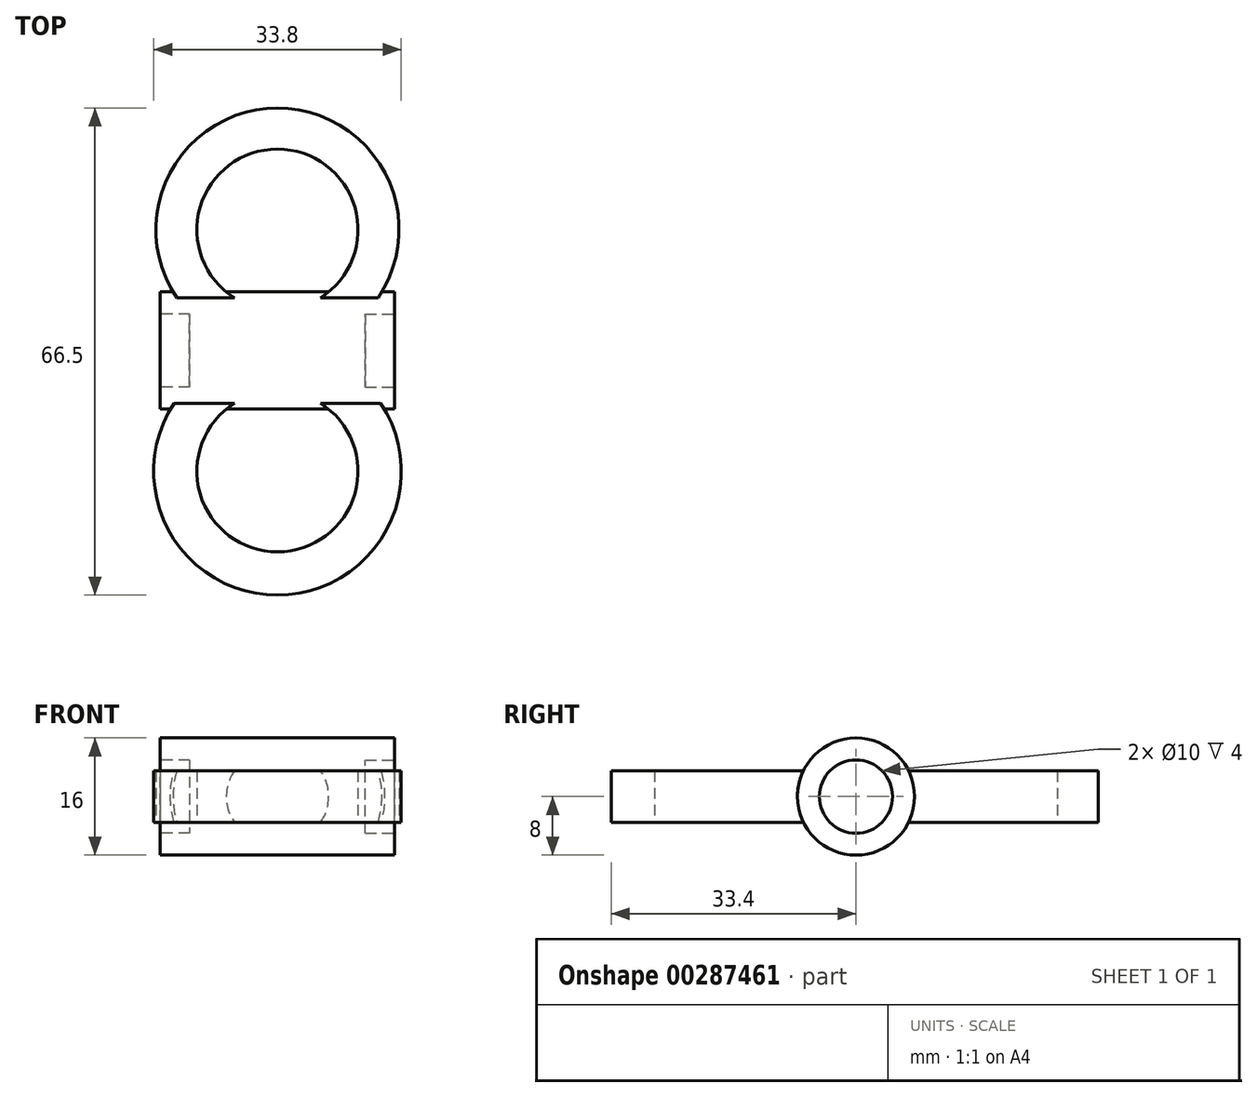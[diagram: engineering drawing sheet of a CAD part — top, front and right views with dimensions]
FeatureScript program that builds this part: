
annotation { "Feature Type Name" : "Feature", "Feature Type Description" : "" }
export const myFeature = defineFeature(function(context is Context, id is Id, definition is map)
    precondition{}
    {
        {
            var Q0;
            Q0=qCreatedBy(makeId("Top.planeOp"),FACE);
            var sketch = newSketch(context, id + "F0", { "sketchPlane" : qUnion([Q0])});
            skCircle(sketch, "E0", {"center": v(0, 0) * mm, "radius": 11 * mm});
            skCircle(sketch, "E1", {"center": v(0, 33) * mm, "radius": 11 * mm});
            skArc(sketch, "E2", {"start": v(13.15, 22.88) * mm, "mid": v(0, 49.6) * mm, "end": v(-13.15, 22.88) * mm});
            skLineSegment(sketch, "E3", {"start": v(0, 16.9) * mm, "end": v(0, 16.65) * mm});
            skArc(sketch, "E4", {"start": v(-13.15, 22.88) * mm, "mid": v(-14.55, 16.72) * mm, "end": v(-13.2, 10.55) * mm});
            skArc(sketch, "E5.trimOffspring", {"start": v(13.2, 10.55) * mm, "mid": v(14.55, 16.72) * mm, "end": v(13.15, 22.88) * mm});
            skArc(sketch, "E6.trimOffspring", {"start": v(-13.2, 10.55) * mm, "mid": v(0, -16.9) * mm, "end": v(13.2, 10.55) * mm});
            skPoint(sketch, "E7.orphan", {"position": v(0, 16.4) * mm});
            skSolve(sketch);
        }
        {
            var Q0;
            Q0=qSketchRegion(id+"F0",true);
            extrude(context, id + "F1", {"entities" : qUnion([Q0]), "depth" : 7 * mm});
        }
        {
            var Q0;
            Q0=qCreatedBy(makeId("Right.planeOp"),FACE);
            var sketch = newSketch(context, id + "F2", { "sketchPlane" : qUnion([Q0])});
            skLineSegment(sketch, "E8", {"start": v(0, 0) * mm, "end": v(0, 7) * mm});
            skLineSegment(sketch, "E9", {"start": v(0, 7) * mm, "end": v(16.5, 7) * mm});
            skLineSegment(sketch, "E10", {"start": v(16.5, 7) * mm, "end": v(16.5, 0) * mm});
            skCircle(sketch, "E11", {"center": v(16.5, 3.5) * mm, "radius": 8 * mm});
            skSolve(sketch);
        }
        {
            var Q0;
            Q0 = qSketchRegion(id + "F2", true);
            extrude(context, id + "F3", {"entities" : qUnion([Q0]), "operationType" : NewBodyOperationType.ADD, "depth" : 16 * mm, "hasSecondDirection" : true, "secondDirectionOppositeDirection" : true, "secondDirectionDepth" : 16 * mm});
        }
        {
            var Q0;
            Q0=makeQuery(id+"F3.opExtrude","CAP_FACE",FACE,{"disambiguationData":[OSD([sQuery(id+"F2.wireOp",EDGE,"E11")])],"isStart":false});
            var sketch = newSketch(context, id + "F4", { "sketchPlane" : qUnion([Q0])});
            skCircle(sketch, "E12", {"center": v(16.5, 3.5) * mm, "radius": 5 * mm});
            skSolve(sketch);
        }
        {
            var Q0;
            Q0 = qSketchRegion(id + "F4", true);
            extrude(context, id + "F5", {"entities" : qUnion([Q0]), "operationType" : NewBodyOperationType.REMOVE, "oppositeDirection" : true, "depth" : 4 * mm});
        }
        {
            var Q0;
            Q0=makeQuery(id+"F3.opExtrude","CAP_FACE",FACE,{"disambiguationData":[OSD([sQuery(id+"F2.wireOp",EDGE,"E11")])],"isStart":true});
            var sketch = newSketch(context, id + "F6", { "sketchPlane" : qUnion([Q0])});
            skCircle(sketch, "E13", {"center": v(-16.5, 3.5) * mm, "radius": 5 * mm});
            skSolve(sketch);
        }
        {
            var Q0;
            Q0 = qSketchRegion(id + "F6", true);
            extrude(context, id + "F7", {"entities" : qUnion([Q0]), "operationType" : NewBodyOperationType.REMOVE, "oppositeDirection" : true, "depth" : 4 * mm});
        }
        {
            var Q0;
            Q0=qCreatedBy(makeId("Top.planeOp"),FACE);
            var sketch = newSketch(context, id + "F8", { "sketchPlane" : qUnion([Q0])});
            skCircle(sketch, "E14", {"center": v(0, 0) * mm, "radius": 11 * mm});
            skLineSegment(sketch, "E15", {"start": v(0, 0) * mm, "end": v(0, 33) * mm});
            skCircle(sketch, "E16", {"center": v(0, 33) * mm, "radius": 11 * mm});
            skSolve(sketch);
        }
        {
            var Q0;
            Q0=makeQuery(id+"F8.imprint","IMPRINT",FACE,{"disambiguationData":[TD([[makeQuery(id+"F8.imprint","IMPRINT",EDGE,{"derivedFrom":sQuery(id+"F8.wireOp",EDGE,"E14")}),1.0]])]});
            var Q1;
            Q1=makeQuery(id+"F8.imprint","IMPRINT",FACE,{"disambiguationData":[TD([[makeQuery(id+"F8.imprint","IMPRINT",EDGE,{"derivedFrom":sQuery(id+"F8.wireOp",EDGE,"E16")}),1.0]])]});
            var Q2;
            Q2=sQuery(id+"F8.wireOp",EDGE,"E16");
            var Q3;
            Q3=sQuery(id+"F8.wireOp",EDGE,"E14");
            extrude(context, id + "F9", {"entities" : qUnion([Q0, Q1]), "operationType" : NewBodyOperationType.REMOVE, "surfaceEntities" : qUnion([Q2, Q3]), "endBound" : BoundingType.SYMMETRIC, "depth" : 25 * mm});
        }
    });
